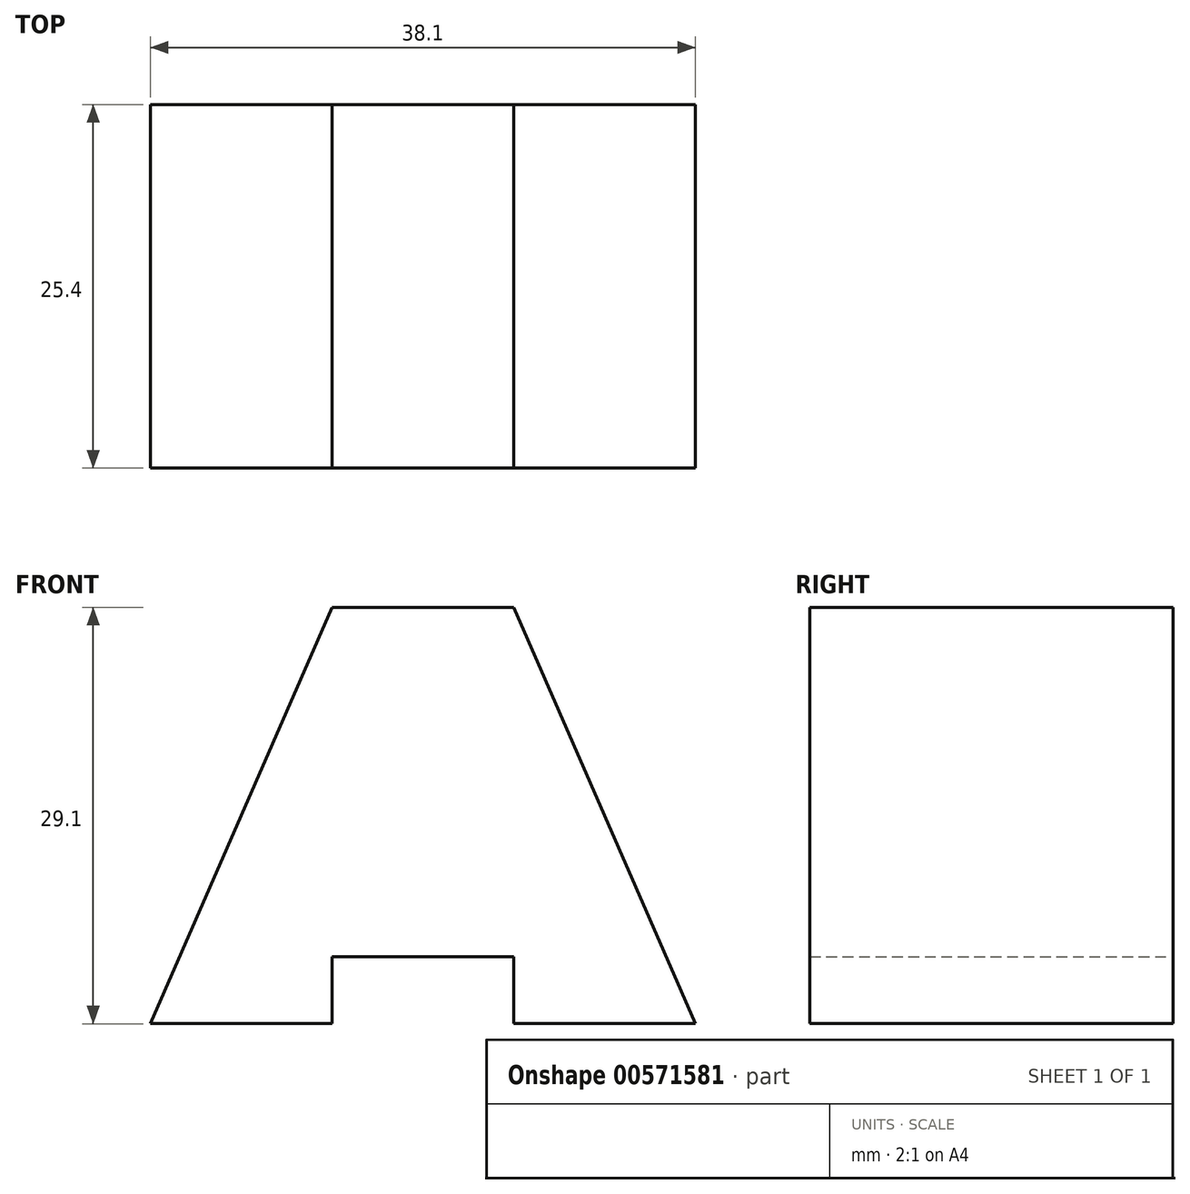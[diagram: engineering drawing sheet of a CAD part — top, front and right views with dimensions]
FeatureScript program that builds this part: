
annotation { "Feature Type Name" : "Feature", "Feature Type Description" : "" }
export const myFeature = defineFeature(function(context is Context, id is Id, definition is map)
    precondition{}
    {
        {
            var Q0;
            Q0=qCreatedBy(makeId("Front.planeOp"),FACE);
            var sketch = newSketch(context, id + "F0", { "sketchPlane" : qUnion([Q0])});
            skLineSegment(sketch, "E0", {"start": v(-34.15, 44.83) * mm, "end": v(-21.45, 44.83) * mm});
            skLineSegment(sketch, "E1", {"start": v(-34.15, 44.83) * mm, "end": v(-46.85, 15.73) * mm});
            skLineSegment(sketch, "E2", {"start": v(-46.85, 15.73) * mm, "end": v(-34.15, 15.73) * mm});
            skLineSegment(sketch, "E3", {"start": v(-34.15, 15.73) * mm, "end": v(-34.15, 20.41) * mm});
            skLineSegment(sketch, "E4", {"start": v(-34.15, 20.41) * mm, "end": v(-21.45, 20.41) * mm});
            skLineSegment(sketch, "E5", {"start": v(-21.45, 20.41) * mm, "end": v(-21.45, 15.73) * mm});
            skLineSegment(sketch, "E6", {"start": v(-21.45, 15.73) * mm, "end": v(-8.75, 15.73) * mm});
            skLineSegment(sketch, "E7", {"start": v(-8.75, 15.73) * mm, "end": v(-21.45, 44.83) * mm});
            skSolve(sketch);
        }
        {
            var Q0;
            Q0=makeQuery(id+"F0.imprint","IMPRINT",FACE,{"disambiguationData":[TD([[makeQuery(id+"F0.imprint","IMPRINT",EDGE,{"derivedFrom":sQuery(id+"F0.wireOp",EDGE,"E0")}),-1.0]])]});
            extrude(context, id + "F1", {"entities" : qUnion([Q0]), "depth" : 25.4 * mm, "offsetDistance" : 25.4 * mm});
        }
    });
